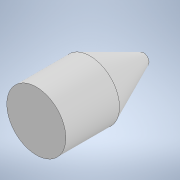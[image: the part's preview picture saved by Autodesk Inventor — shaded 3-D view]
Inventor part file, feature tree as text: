
AUTODESK INVENTOR PART (.ipt)
format: ipt  version: 2021 (Build 250183000, 183)  size: 104,448 bytes
history: native  units: mm
features: sketch x2, extrude x1, plane x1, loft x1, other x1
ambient origin geometry x8: Origin, YZ Plane, XZ Plane, XY Plane, X Axis, Y Axis, Z Axis, Center Point
bodies: Solid1 (feature_tree)
feature tree (6):
  extrude  "Extrusion1"  Depth=10.0mm TaperAngle=0.0deg
  plane  "Work Plane1"
  loft  "Loft1"
  sketch  "Sketch1"  dims[d0=11.0mm d1=10.0mm d2=0.0mm]
  sketch  "Sketch2"  dims[d3=10.0mm d4=2.0mm d5=0.0mm d6=90.0deg d7=0.0mm d8=90.0deg]
  other  "Edges1"
